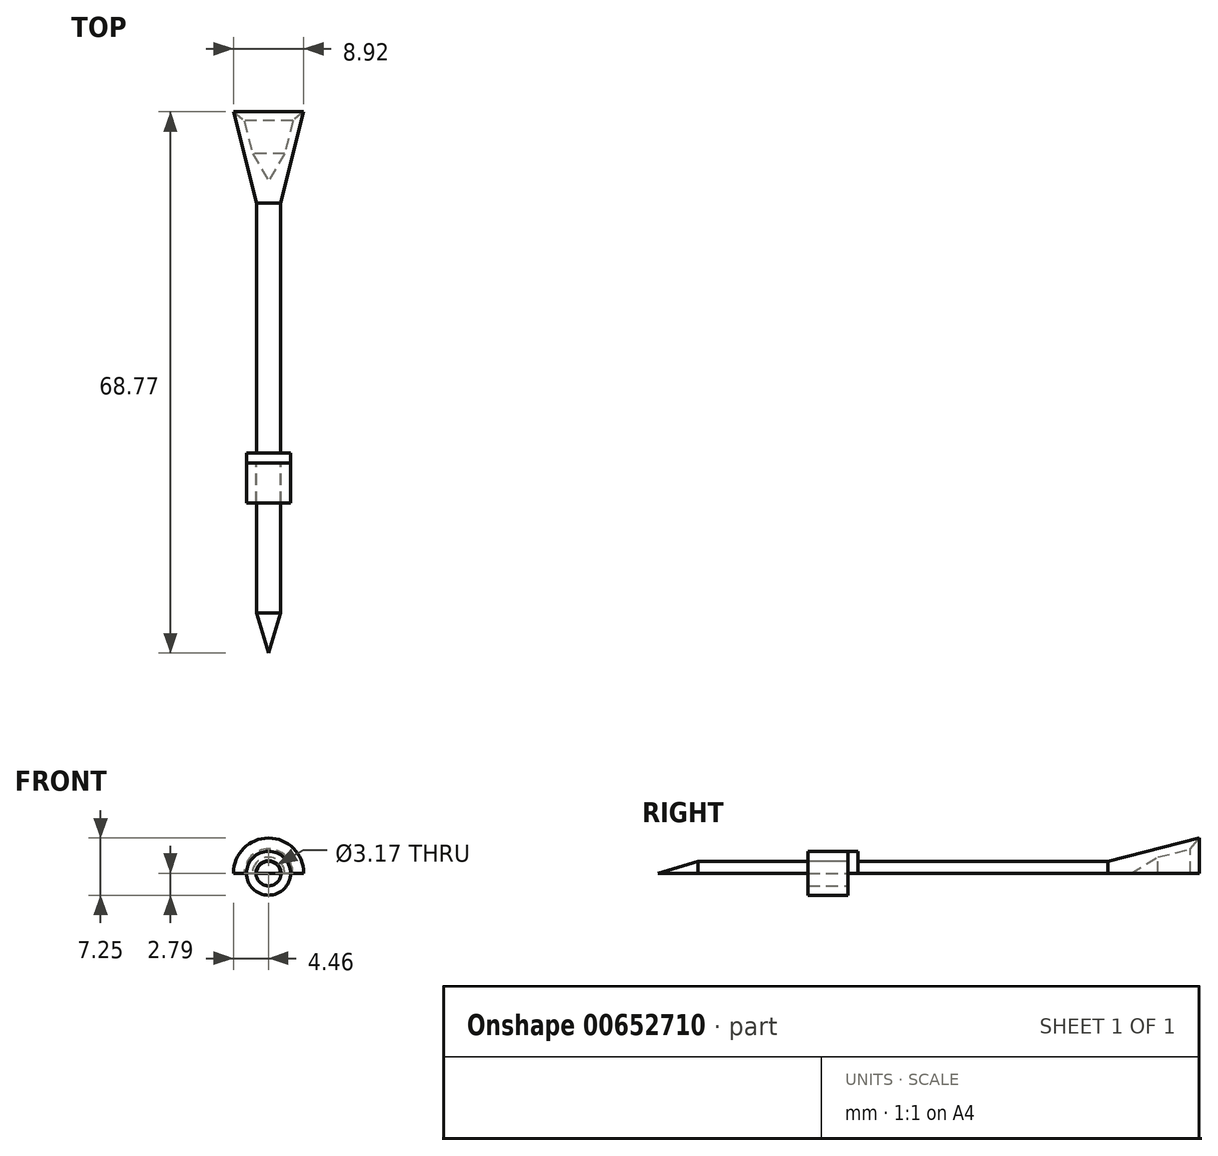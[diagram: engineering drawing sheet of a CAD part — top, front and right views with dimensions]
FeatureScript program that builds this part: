
annotation { "Feature Type Name" : "Feature", "Feature Type Description" : "" }
export const myFeature = defineFeature(function(context is Context, id is Id, definition is map)
    precondition{}
    {
        {
            var Q0;
            Q0=qCreatedBy(makeId("Top.planeOp"),FACE);
            var sketch = newSketch(context, id + "F0", { "sketchPlane" : qUnion([Q0])});
            skLineSegment(sketch, "E0", {"start": v(0, 0) * mm, "end": v(0, 60.03) * mm});
            skLineSegment(sketch, "E1", {"start": v(-1.52, 5.08) * mm, "end": v(0, 0) * mm});
            skLineSegment(sketch, "E2", {"start": v(-1.52, 5.08) * mm, "end": v(-1.52, 24.13) * mm});
            skLineSegment(sketch, "E3", {"start": v(-1.52, 57.15) * mm, "end": v(-4.46, 68.77) * mm});
            skLineSegment(sketch, "E4", {"start": v(-1.52, 25.4) * mm, "end": v(-2.8, 25.4) * mm});
            skLineSegment(sketch, "E5", {"start": v(-2.8, 25.4) * mm, "end": v(-2.8, 24.13) * mm});
            skLineSegment(sketch, "E6", {"start": v(-2.8, 24.13) * mm, "end": v(-1.52, 24.13) * mm});
            skLineSegment(sketch, "E7.trimOffspring", {"start": v(-1.52, 25.4) * mm, "end": v(-1.52, 57.15) * mm});
            skLineSegment(sketch, "E8", {"start": v(-4.46, 68.77) * mm, "end": v(-3.1, 67.62) * mm});
            skLineSegment(sketch, "E9", {"start": v(-3.1, 67.62) * mm, "end": v(-2.04, 63.47) * mm});
            skLineSegment(sketch, "E10", {"start": v(-2.04, 63.47) * mm, "end": v(0, 60.03) * mm});
            skPoint(sketch, "E11.orphan", {"position": v(0, 63.5) * mm});
            skSolve(sketch);
        }
        {
            var Q0;
            Q0=makeQuery(id+"F0.imprint","IMPRINT",FACE,{"disambiguationData":[TD([[makeQuery(id+"F0.imprint","IMPRINT",EDGE,{"derivedFrom":sQuery(id+"F0.wireOp",EDGE,"E0")}),1.0]])]});
            var Q1;
            Q1=sQuery(id+"F0.wireOp",EDGE,"E0");
            revolve(context, id + "F1", {"entities" : qUnion([Q0]), "axis" : qUnion([Q1]), "revolveType" : RevolveType.ONE_DIRECTION, "angle" : 180 * degree});
        }
        {
            var Q0;
            Q0=makeQuery(id+"F1.opRevolve","SWEPT_FACE",FACE,{"disambiguationData":[OSD([sQuery(id+"F0.wireOp",EDGE,"E6")])]});
            var sketch = newSketch(context, id + "F2", { "sketchPlane" : qUnion([Q0])});
            skCircle(sketch, "E12", {"center": v(0, 0) * mm, "radius": 2.8 * mm});
            skCircle(sketch, "E13", {"center": v(0, 0) * mm, "radius": 1.59 * mm});
            skSolve(sketch);
        }
        {
            var Q0;
            {var subQ0=sQuery(id+"F2.wireOp",EDGE,"E12");var subQ1=sQuery(id+"F0.wireOp",EDGE,"E6");var subQ2=makeQuery(id+"F1.opRevolve","CAP_EDGE",EDGE,{"disambiguationData":[OSD([subQ1])],"isStart":true});var subQ3=makeQuery(id+"F2.imprint","INTERSECT",VERTEX,{"derivedFrom":[subQ2,subQ0]});Q0=makeQuery(id+"F2.imprint","IMPRINT",FACE,{"disambiguationData":[TD([[makeQuery(id+"F2.imprint","IMPRINT",EDGE,{"disambiguationData":[TD([[subQ3,-1.0]])],"derivedFrom":subQ0}),1.0]])]});}
            var Q1;
            {var subQ0=sQuery(id+"F2.wireOp",EDGE,"E12");var subQ1=sQuery(id+"F0.wireOp",EDGE,"E6");var subQ2=makeQuery(id+"F1.opRevolve","CAP_EDGE",EDGE,{"disambiguationData":[OSD([subQ1])],"isStart":true});var subQ3=makeQuery(id+"F2.imprint","INTERSECT",VERTEX,{"derivedFrom":[subQ2,subQ0]});Q1=makeQuery(id+"F2.imprint","IMPRINT",FACE,{"disambiguationData":[TD([[makeQuery(id+"F2.imprint","IMPRINT",EDGE,{"disambiguationData":[TD([[subQ3,1.0]])],"derivedFrom":subQ0}),1.0]])]});}
            extrude(context, id + "F3", {"entities" : qUnion([Q0, Q1]), "depth" : 5.08 * mm, "offsetDistance" : 25.4 * mm});
        }
    });
